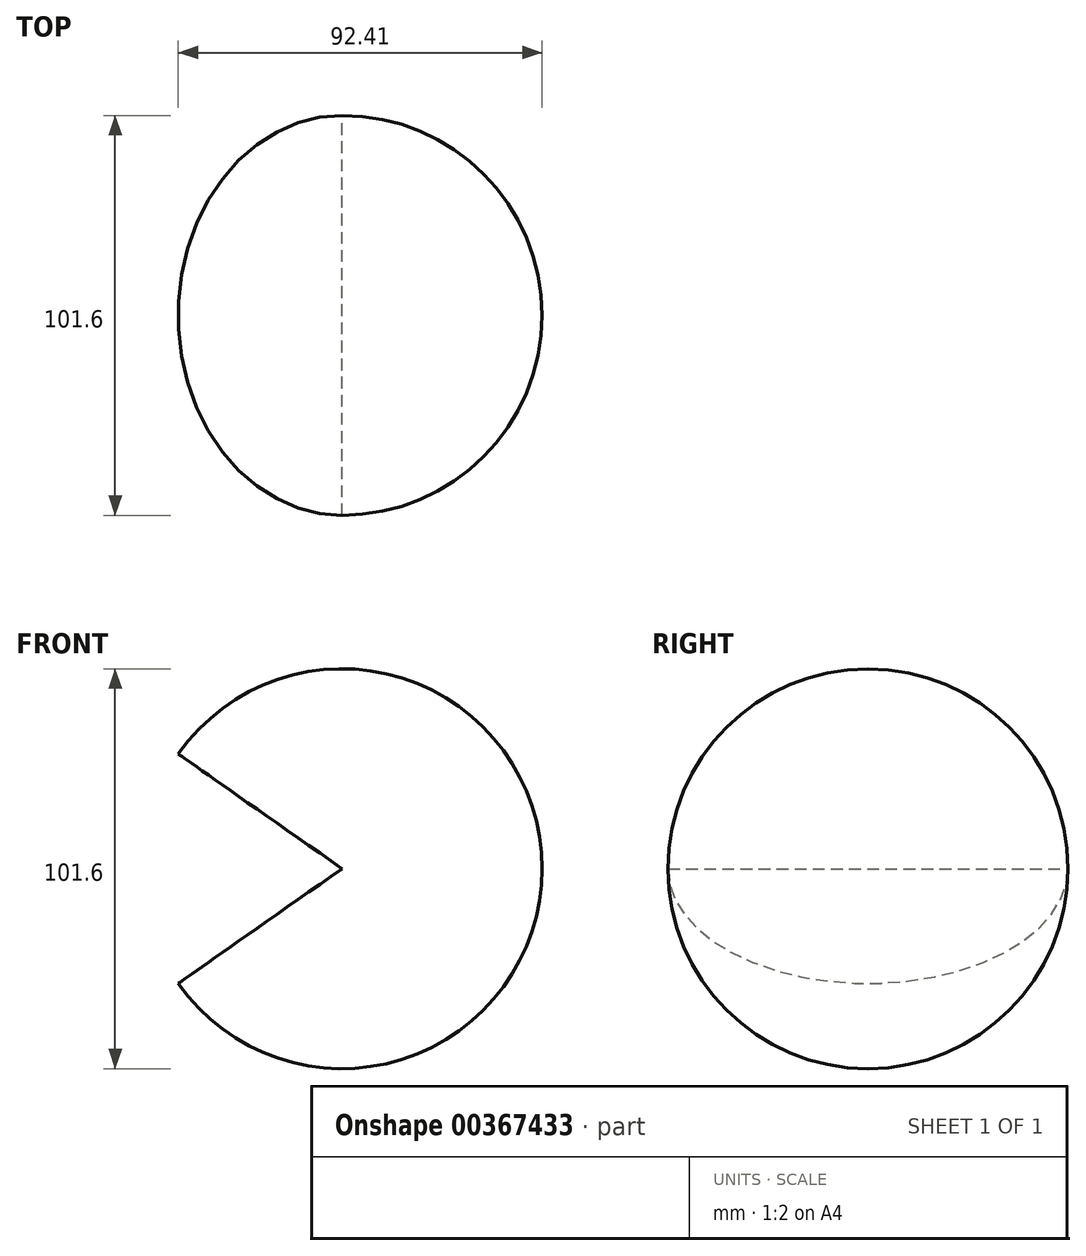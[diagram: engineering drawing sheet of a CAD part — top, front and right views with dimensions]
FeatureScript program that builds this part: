
annotation { "Feature Type Name" : "Feature", "Feature Type Description" : "" }
export const myFeature = defineFeature(function(context is Context, id is Id, definition is map)
    precondition{}
    {
        {
            var Q0;
            Q0=qCreatedBy(makeId("Top.planeOp"),FACE);
            var sketch = newSketch(context, id + "F0", { "sketchPlane" : qUnion([Q0])});
            skLineSegment(sketch, "E0", {"start": v(0, 0) * mm, "end": v(0, 50.8) * mm});
            skArc(sketch, "E1", {"start": v(0, 50.8) * mm, "mid": v(50.8, 0) * mm, "end": v(0, -50.8) * mm});
            skLineSegment(sketch, "E2", {"start": v(0, -50.8) * mm, "end": v(0, 0) * mm});
            skSolve(sketch);
        }
        {
            var Q0;
            Q0=makeQuery(id+"F0.imprint","IMPRINT",FACE,{"disambiguationData":[TD([[makeQuery(id+"F0.imprint","IMPRINT",EDGE,{"derivedFrom":sQuery(id+"F0.wireOp",EDGE,"E0")}),-1.0]])]});
            var Q1;
            Q1=sQuery(id+"F0.wireOp",EDGE,"E0");
            revolve(context, id + "F1", {"entities" : qUnion([Q0]), "axis" : qUnion([Q1]), "revolveType" : RevolveType.SYMMETRIC, "angle" : 290 * degree});
        }
    });
